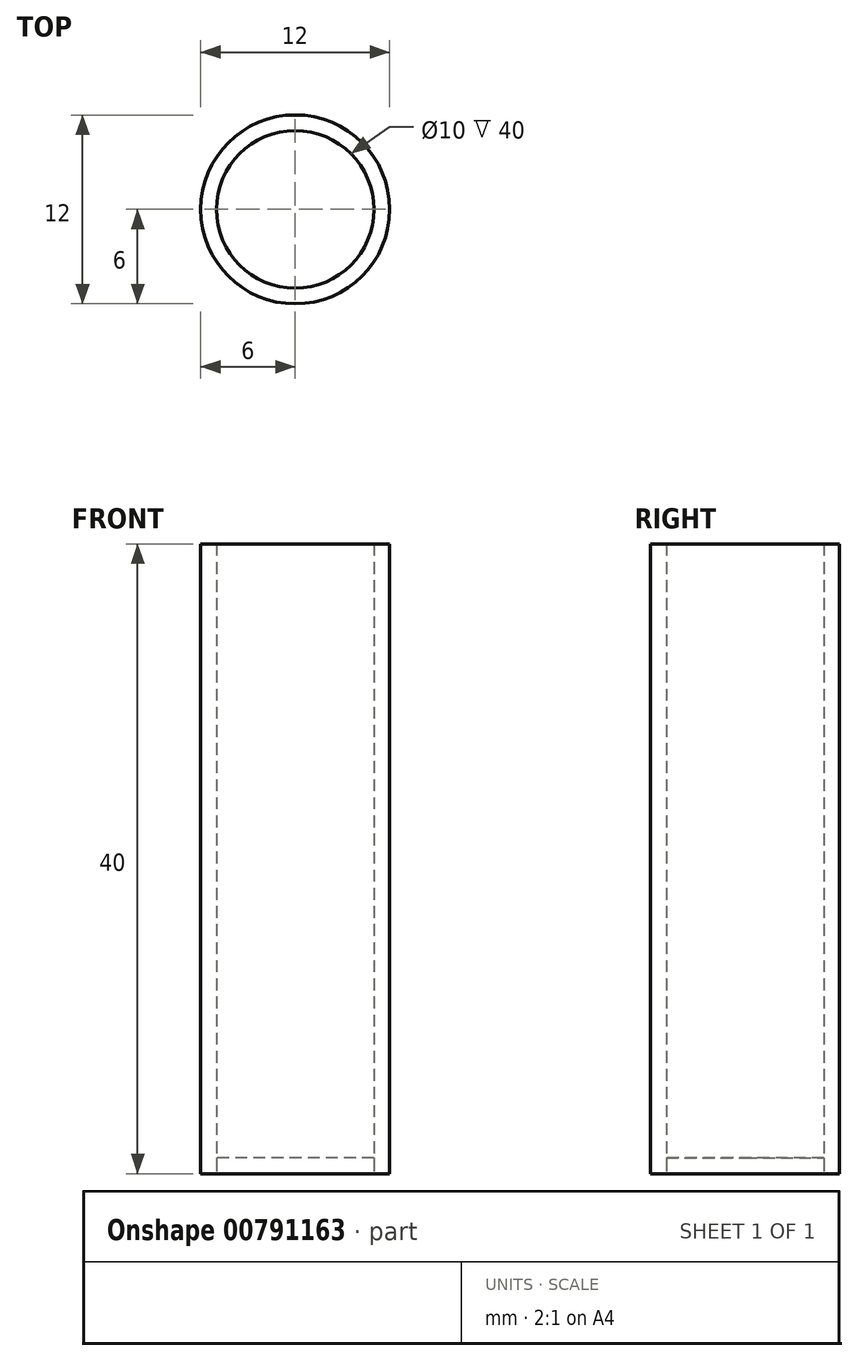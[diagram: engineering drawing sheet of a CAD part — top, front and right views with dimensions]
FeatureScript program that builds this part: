
annotation { "Feature Type Name" : "Feature", "Feature Type Description" : "" }
export const myFeature = defineFeature(function(context is Context, id is Id, definition is map)
    precondition{}
    {
        {
            var Q0;
            Q0=qCreatedBy(makeId("Top.planeOp"),FACE);
            var sketch = newSketch(context, id + "F0", { "sketchPlane" : qUnion([Q0])});
            skCircle(sketch, "E0", {"center": v(0, 0) * mm, "radius": 6 * mm});
            skCircle(sketch, "E1", {"center": v(0, 0) * mm, "radius": 5 * mm});
            skSolve(sketch);
        }
        {
            var Q0;
            Q0=makeQuery(id+"F0.imprint","IMPRINT",FACE,{"disambiguationData":[TD([[makeQuery(id+"F0.imprint","IMPRINT",EDGE,{"derivedFrom":sQuery(id+"F0.wireOp",EDGE,"E0")}),1.0]])]});
            extrude(context, id + "F1", {"entities" : qUnion([Q0]), "depth" : 40 * mm, "offsetDistance" : 25.4 * mm});
        }
        {
            var Q0;
            Q0=makeQuery(id+"F0.imprint","IMPRINT",FACE,{"disambiguationData":[TD([[makeQuery(id+"F0.imprint","IMPRINT",EDGE,{"derivedFrom":sQuery(id+"F0.wireOp",EDGE,"E1")}),1.0]])]});
            extrude(context, id + "F2", {"entities" : qUnion([Q0]), "depth" : 1 * mm, "offsetDistance" : 25.4 * mm});
        }
    });
